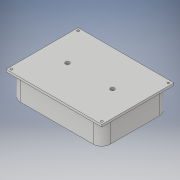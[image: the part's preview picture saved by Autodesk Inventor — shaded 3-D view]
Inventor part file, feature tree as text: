
AUTODESK INVENTOR PART (.ipt)
format: ipt  version: 2018 (Build 220112000, 112)  size: 311,808 bytes
history: native  units: in
note: dims shown in document units (in); Inventor stores cm internally (conversion verified against a paired STEP export)
features: extrude x11, sketch x7, projected_geometry x7, fillet x1, chamfer x1
ambient origin geometry x8: Origin, YZ Plane, XZ Plane, XY Plane, X Axis, Y Axis, Z Axis, Center Point
bodies: Solid1 (feature_tree)
feature tree (27):
  sketch  "Sketch1"  dims[d0=9.125in d1=0.5in]
  extrude  "Extrusion1"  Depth=0.5in
  extrude  "Extrusion2"  Depth=0.25in
  fillet  "Fillet1"  Radius=0.25in
  sketch  "Sketch2"  dims[d2=0.5in d3=6.5in d4=0.25in]
  extrude  "Extrusion3"  Depth=2.3622in TaperAngle=0.0deg
  extrude  "Extrusion4"  Depth=1.0in
  extrude  "Extrusion5"  Depth=0.5in
  extrude  "Extrusion6"  Depth=0.5in
  sketch  "Sketch5"  dims[d11=2.25in d12=0.5in]
  extrude  "Extrusion7"  Depth=0.5in
  extrude  "Extrusion8"  Depth=0.5in
  extrude  "Extrusion9"  Depth=2.179in
  extrude  "Extrusion10"  Depth=1.0in TaperAngle=0.0deg
  chamfer  "Chamfer2"  Distance=0.125in
  extrude  "Extrusion11"  Depth=1.0in
  sketch  "Sketch3"  dims[d5=2.3622in d6=0.0in d7=0.6in d8=0.0in]
  projected_geometry  "Projected Loop1"
  sketch  "Sketch4"  dims[d9=1.0in d10=3.5in]
  projected_geometry  "Projected Loop2"
  projected_geometry  "Projected Loop3"
  projected_geometry  "Projected Loop4"
  projected_geometry  "Projected Loop5"
  projected_geometry  "Projected Loop6"
  sketch  "Sketch6"  dims[d13=0.5in d14=0.5in]
  sketch  "Sketch7"  dims[d15=0.5in d17=0.5in d18=0.5in d19=0.45in d20=1.0in d21=0.0in d22=0.125in d23=0.0in d24=1.0in d25=1.0in d26=1.0in d27=0.125in d28=0.0in d29=0.125in d30=0.0in d31=0.25in d32=0.3in d33=0.3in d34=0.3in d35=0.3in d36=1.0in d37=0.0in d38=0.25in d39=0.0in d40=0.25in d41=0.0in d42=2.5in d43=2.5in d44=0.45in d45=0.45in d46=0.25in d47=0.0in d51=0.0625in d52=0.125in d53=45.0deg d54=0.375in d55=2.179in d56=0.0in]
  projected_geometry  "Projected Loop7"
